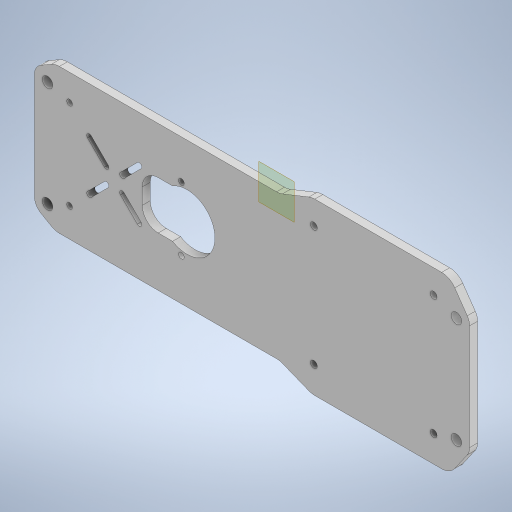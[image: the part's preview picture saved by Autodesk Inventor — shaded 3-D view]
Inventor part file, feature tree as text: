
AUTODESK INVENTOR PART (.ipt)
format: ipt  version: 2024 (Build 280153000, 153)  size: 447,488 bytes
history: native  units: in
note: dims shown in document units (in); Inventor stores cm internally (conversion verified against a paired STEP export)
features: other x4, extrude x1
ambient origin geometry x8: Origin, YZ Plane, XZ Plane, XY Plane, X Axis, Y Axis, Z Axis, Center Point
bodies: Body1 (feature_tree)
feature tree (5):
  other  "作業平面1"
  other  "Base_plate"
  other  "RPLidarA1M8"
  other  "RPLidarA2M6"
  extrude  "押し出し1"  Depth=0.1181in
